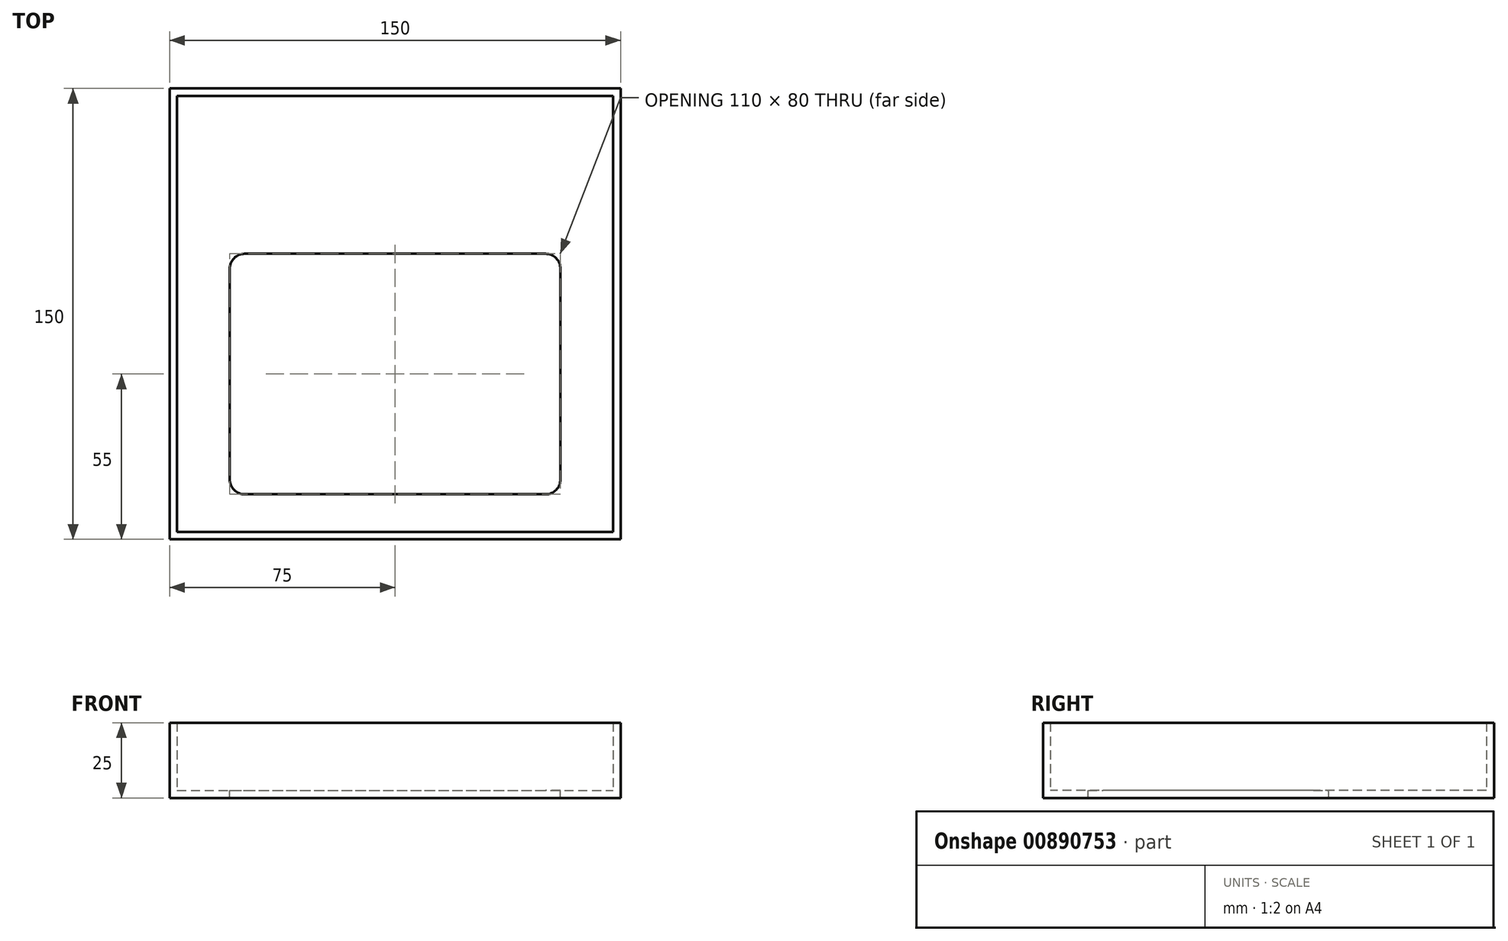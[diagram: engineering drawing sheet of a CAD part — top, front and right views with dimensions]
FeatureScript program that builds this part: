
annotation { "Feature Type Name" : "Feature", "Feature Type Description" : "" }
export const myFeature = defineFeature(function(context is Context, id is Id, definition is map)
    precondition{}
    {
        {
            var Q0;
            Q0=qCreatedBy(makeId("Top.planeOp"),FACE);
            var sketch = newSketch(context, id + "F0", { "sketchPlane" : qUnion([Q0])});
            skLineSegment(sketch, "E0.bottom", {"start": v(-75, 75) * mm, "end": v(75, 75) * mm});
            skLineSegment(sketch, "E0.top", {"start": v(-75, -75) * mm, "end": v(75, -75) * mm});
            skLineSegment(sketch, "E0.left", {"start": v(-75, 75) * mm, "end": v(-75, -75) * mm});
            skLineSegment(sketch, "E0.right", {"start": v(75, 75) * mm, "end": v(75, -75) * mm});
            skLineSegment(sketch, "E1", {"start": v(-75, 0) * mm, "end": v(75, 0) * mm, "construction": true});
            skSolve(sketch);
        }
        {
            var Q0;
            Q0 = qSketchRegion(id + "F0", true);
            extrude(context, id + "F1", {"entities" : qUnion([Q0]), "depth" : 25 * mm, "offsetDistance" : 25 * mm});
        }
        {
            var Q0;
            Q0=makeQuery(id+"F1.opExtrude","CAP_FACE",FACE,{"disambiguationData":[OSD([sQuery(id+"F0.wireOp",EDGE,"E0.bottom"),sQuery(id+"F0.wireOp",EDGE,"E0.top"),sQuery(id+"F0.wireOp",EDGE,"E0.left"),sQuery(id+"F0.wireOp",EDGE,"E0.right")])],"isStart":false});
            shell(context, id + "F2", {"entities" : qUnion([Q0]), "thickness" : 2.5 * mm});
        }
        {
            var Q0;
            Q0=makeQuery(id+"F2.opShell","OFFSET_FACE",FACE,{"disambiguationData":[OSD([sQuery(id+"F0.wireOp",EDGE,"E0.bottom"),sQuery(id+"F0.wireOp",EDGE,"E0.top"),sQuery(id+"F0.wireOp",EDGE,"E0.left"),sQuery(id+"F0.wireOp",EDGE,"E0.right")])]});
            var sketch = newSketch(context, id + "F3", { "sketchPlane" : qUnion([Q0])});
            skLineSegment(sketch, "E2.bottom", {"start": v(-50, 20) * mm, "end": v(50, 20) * mm});
            skLineSegment(sketch, "E2.top", {"start": v(-50, -60) * mm, "end": v(50, -60) * mm});
            skLineSegment(sketch, "E2.left", {"start": v(-55, 15) * mm, "end": v(-55, -55) * mm});
            skLineSegment(sketch, "E2.right", {"start": v(55, 15) * mm, "end": v(55, -55) * mm});
            skPoint(sketch, "E3.visualSharp", {"position": v(-55, 20) * mm});
            skArc(sketch, "E3.filletArc", {"start": v(-50, 20) * mm, "mid": v(-53.54, 18.54) * mm, "end": v(-55, 15) * mm});
            skPoint(sketch, "E4.visualSharp", {"position": v(55, 20) * mm});
            skArc(sketch, "E4.filletArc", {"start": v(55, 15) * mm, "mid": v(53.54, 18.54) * mm, "end": v(50, 20) * mm});
            skPoint(sketch, "E5.visualSharp", {"position": v(55, -60) * mm});
            skArc(sketch, "E5.filletArc", {"start": v(50, -60) * mm, "mid": v(53.54, -58.54) * mm, "end": v(55, -55) * mm});
            skPoint(sketch, "E6.visualSharp", {"position": v(-55, -60) * mm});
            skArc(sketch, "E6.filletArc", {"start": v(-55, -55) * mm, "mid": v(-53.54, -58.54) * mm, "end": v(-50, -60) * mm});
            skLineSegment(sketch, "E7", {"start": v(0, 20) * mm, "end": v(0, -60) * mm, "construction": true});
            skSolve(sketch);
        }
        {
            var Q0;
            Q0 = qSketchRegion(id + "F3", true);
            extrude(context, id + "F4", {"entities" : qUnion([Q0]), "operationType" : NewBodyOperationType.REMOVE, "oppositeDirection" : true, "depth" : 25 * mm, "offsetDistance" : 25 * mm});
        }
    });
